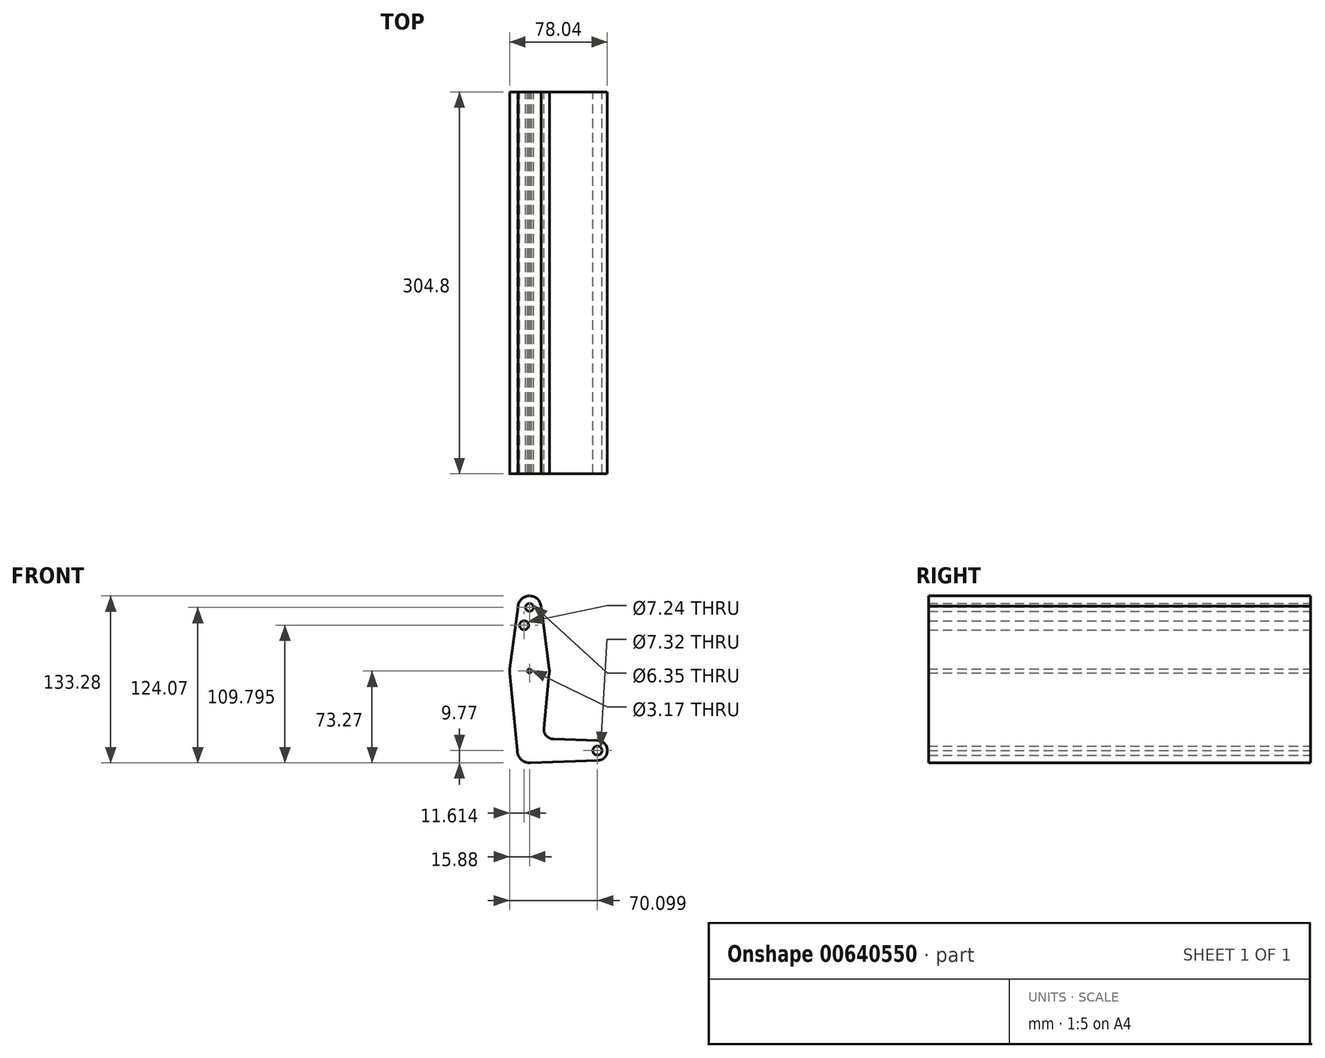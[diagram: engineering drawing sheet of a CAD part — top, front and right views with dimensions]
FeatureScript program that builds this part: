
annotation { "Feature Type Name" : "Feature", "Feature Type Description" : "" }
export const myFeature = defineFeature(function(context is Context, id is Id, definition is map)
    precondition{}
    {
        {
            var Q0;
            Q0=qCreatedBy(makeId("Front.planeOp"),FACE);
            var sketch = newSketch(context, id + "F0", { "sketchPlane" : qUnion([Q0])});
            skLineSegment(sketch, "E0", {"start": v(0, 0) * mm, "end": v(0, 114.3) * mm, "construction": true});
            skLineSegment(sketch, "E1", {"start": v(0, 0) * mm, "end": v(54.22, 0) * mm, "construction": true});
            skCircle(sketch, "E2", {"center": v(0, 114.3) * mm, "radius": 9.2 * mm});
            skCircle(sketch, "E3", {"center": v(0, 63.5) * mm, "radius": 15.88 * mm});
            skCircle(sketch, "E4", {"center": v(0, 0) * mm, "radius": 9.77 * mm});
            skCircle(sketch, "E5", {"center": v(54.22, 0) * mm, "radius": 7.94 * mm});
            skLineSegment(sketch, "E6", {"start": v(-9.2, 114.68) * mm, "end": v(-15.74, 65.6) * mm});
            skLineSegment(sketch, "E7", {"start": v(9.17, 115.16) * mm, "end": v(15.74, 65.59) * mm});
            skLineSegment(sketch, "E8", {"start": v(19.07, 9.13) * mm, "end": v(54.49, 7.93) * mm});
            skLineSegment(sketch, "E9", {"start": v(0, -9.77) * mm, "end": v(54.49, -7.93) * mm});
            skCircle(sketch, "E10", {"center": v(0, 114.3) * mm, "radius": 3.18 * mm});
            skCircle(sketch, "E11", {"center": v(0, 63.5) * mm, "radius": 1.59 * mm});
            skCircle(sketch, "E12", {"center": v(54.22, 0) * mm, "radius": 3.66 * mm});
            skCircle(sketch, "E13", {"center": v(-4.27, 100.03) * mm, "radius": 3.62 * mm});
            skArc(sketch, "E14.filletArc", {"start": v(11.42, 17.79) * mm, "mid": v(13.38, 11.8) * mm, "end": v(19.07, 9.13) * mm});
            skLineSegment(sketch, "E15", {"start": v(-9.77, 0) * mm, "end": v(-15.8, 61.96) * mm});
            skLineSegment(sketch, "E16", {"start": v(11.42, 17.79) * mm, "end": v(15.8, 61.93) * mm});
            skSolve(sketch);
        }
        {
            var Q0;
            Q0 = qSketchRegion(id + "F0", true);
            extrude(context, id + "F1", {"entities" : qUnion([Q0]), "depth" : 304.8 * mm, "offsetDistance" : 25.4 * mm});
        }
    });
